# Revit family: ifö Sign wallhung WC 6875
name_source: partatom
category: Generic Models
revit_build: Autodesk Revit 2015 (Build: 20140606_1530(x64)
units: mm (PartAtom-declared; Revit-internal decimal feet)

## types (1)
- Ifö Sign wallhung WC 6875
    BIMObjectName = ifö Sign wallhung WC 6875
    Brand = Ifö
    Category = WC
    ColdWaterConnectionDiameter = 0.00 mm
    ColdWaterConnectionHeight = 0.00 mm
    Color = White
    ConnectorIn_HDistance = 100.00 mm
    ConnectorOut_VDistance = 250.00 mm
    Depth = 490.00 mm
    Description = Ifö Sign wallhung WC 6875
    DrainSize = 0.00 mm
    Features = feature1, feature2, feature38
    Finish = Glazed
    Height = 360.00 mm
    Manufacturer = Geberit
    Material = Porcelain
    Model = Ifö Sign WC 6875
    ModelNumber = 6875
    ModelReference = Sign
    MountingHeight(offset) = 420.00 mm
    Name = Ifö Sign wallhung WC 6875
    NominalDepth = 490.00 mm
    NominalHeight = 360.00 mm
    NominalWidth = 355.00 mm
    Seatnotincluded(option) = Yes
    Serie = Sign
    Size = 355x360x490
    Type = Building element
    URL.dk = http://www.ifo.dk
    URL.no = http://www.ifosanitar.no
    URL.se = http://www.ifo.se
    WasteConnectionDiameter = 110.00 mm
    Width = 355.00 mm
    WithSeat = Yes
    WithoutSeat = No
    ifcExportAs = ifcSanitaryTerminalType
    ifcExportType = TOILETPAN

## geometry (parser evidence)
native form markers: Blend x10, Sweep x10
no freeform markers — native parametric forms only
